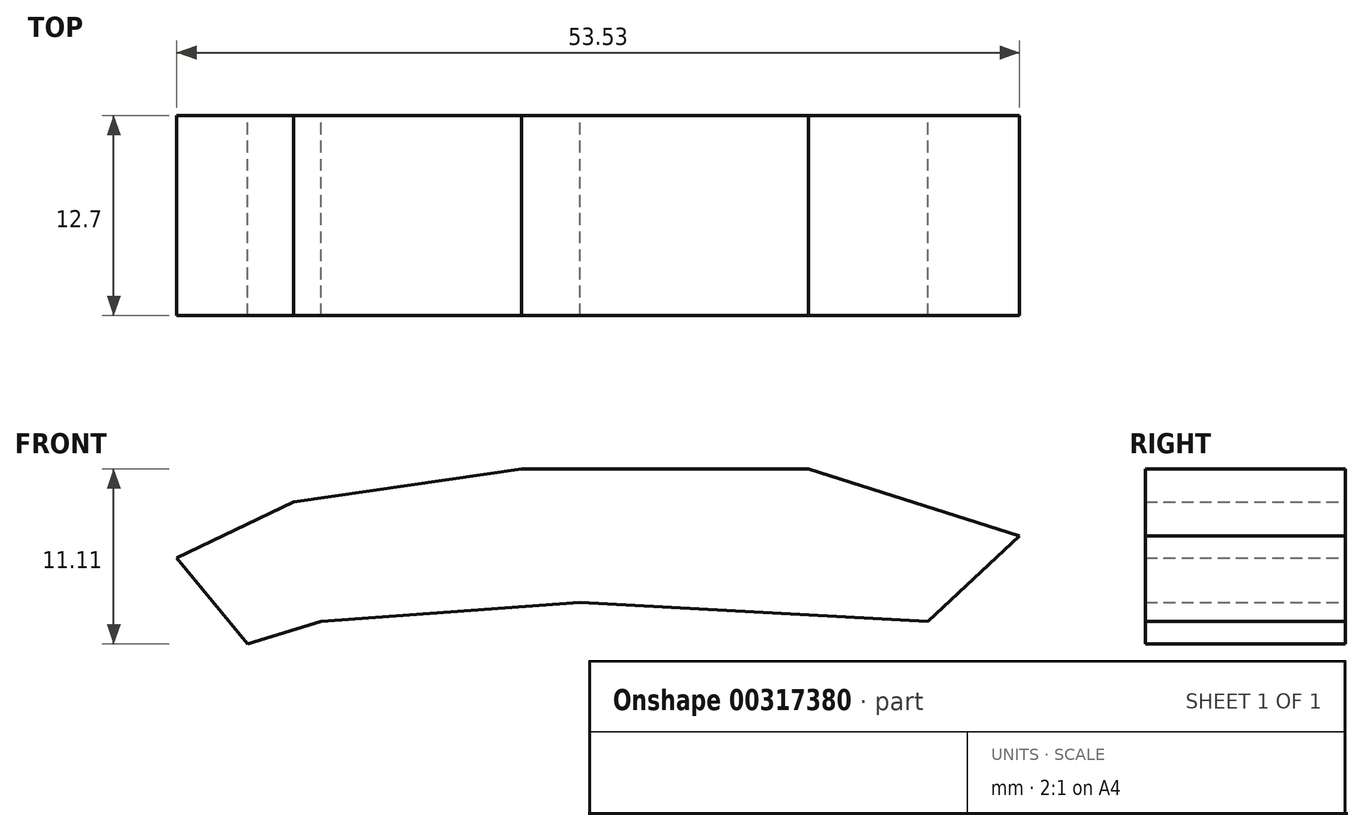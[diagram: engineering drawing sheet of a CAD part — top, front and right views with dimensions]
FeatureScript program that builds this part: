
annotation { "Feature Type Name" : "Feature", "Feature Type Description" : "" }
export const myFeature = defineFeature(function(context is Context, id is Id, definition is map)
    precondition{}
    {
        {
            var Q0;
            Q0=qCreatedBy(makeId("Front.planeOp"),FACE);
            var sketch = newSketch(context, id + "F0", { "sketchPlane" : qUnion([Q0])});
            skLineSegment(sketch, "E0", {"start": v(0, 0) * mm, "end": v(22.08, -1.2) * mm});
            skLineSegment(sketch, "E1", {"start": v(0, 0) * mm, "end": v(-16.44, -1.2) * mm});
            skLineSegment(sketch, "E2", {"start": v(-16.44, -1.2) * mm, "end": v(-22.72, -3.14) * mm});
            skLineSegment(sketch, "E3", {"start": v(22.08, -1.2) * mm, "end": v(27.91, 4.2) * mm});
            skLineSegment(sketch, "E4", {"start": v(27.91, 4.2) * mm, "end": v(14.5, 8.46) * mm});
            skLineSegment(sketch, "E5", {"start": v(14.5, 8.46) * mm, "end": v(-3.7, 8.46) * mm});
            skLineSegment(sketch, "E6", {"start": v(-3.7, 8.46) * mm, "end": v(-18.2, 6.37) * mm});
            skLineSegment(sketch, "E7", {"start": v(-18.2, 6.37) * mm, "end": v(-25.62, 2.82) * mm});
            skLineSegment(sketch, "E8", {"start": v(-25.62, 2.82) * mm, "end": v(-21.11, -2.65) * mm});
            skSolve(sketch);
        }
        {
            var Q0;
            Q0=makeQuery(id+"F0.imprint","IMPRINT",FACE,{"disambiguationData":[TD([[makeQuery(id+"F0.imprint","IMPRINT",EDGE,{"derivedFrom":sQuery(id+"F0.wireOp",EDGE,"E0")}),1.0]])]});
            extrude(context, id + "F1", {"entities" : qUnion([Q0]), "depth" : 12.7 * mm});
        }
    });
